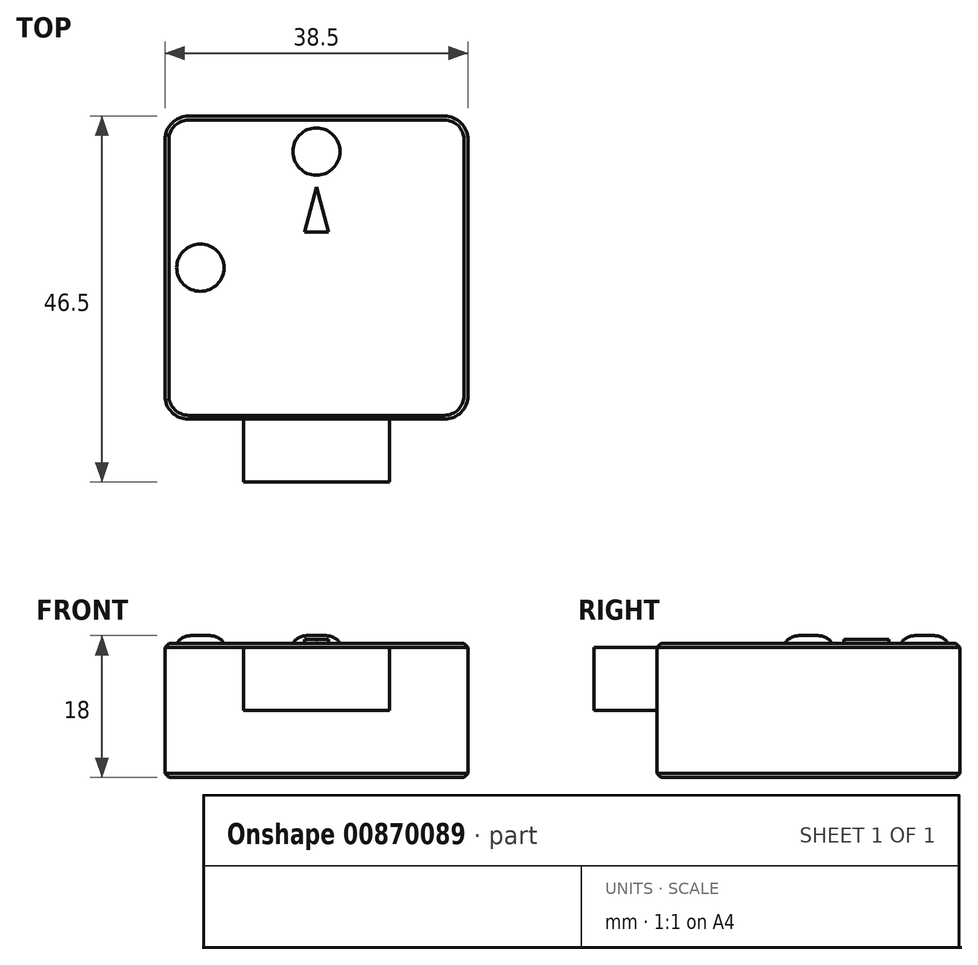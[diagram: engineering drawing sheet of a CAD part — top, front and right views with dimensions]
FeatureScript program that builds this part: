
annotation { "Feature Type Name" : "Feature", "Feature Type Description" : "" }
export const myFeature = defineFeature(function(context is Context, id is Id, definition is map)
    precondition{}
    {
        {
            var Q0;
            Q0=qCreatedBy(makeId("Top.planeOp"),FACE);
            var sketch = newSketch(context, id + "F0", { "sketchPlane" : qUnion([Q0])});
            skLineSegment(sketch, "E0.bottom", {"start": v(19.25, -19.25) * mm, "end": v(-19.25, -19.25) * mm});
            skLineSegment(sketch, "E0.top", {"start": v(19.25, 19.25) * mm, "end": v(-19.25, 19.25) * mm});
            skLineSegment(sketch, "E0.left", {"start": v(19.25, -19.25) * mm, "end": v(19.25, 19.25) * mm});
            skLineSegment(sketch, "E0.right", {"start": v(-19.25, -19.25) * mm, "end": v(-19.25, 19.25) * mm});
            skPoint(sketch, "E0.middle", {"position": v(0, 0) * mm});
            skCircle(sketch, "E1", {"center": v(0, 14.75) * mm, "radius": 3 * mm});
            skCircle(sketch, "E2", {"center": v(-14.75, 0) * mm, "radius": 3 * mm});
            skLineSegment(sketch, "E3", {"start": v(0, 19.25) * mm, "end": v(0, 17.75) * mm});
            skLineSegment(sketch, "E4", {"start": v(-19.25, 0) * mm, "end": v(-17.75, 0) * mm});
            skSolve(sketch);
        }
        {
            var Q0;
            {var subQ5=sQuery(id+"F0.wireOp",EDGE,"E0.bottom");Q0=makeQuery(id+"F0.imprint","IMPRINT",FACE,{"disambiguationData":[TD([[makeQuery(id+"F0.imprint","IMPRINT",EDGE,{"derivedFrom":subQ5}),-1.0]])]});}
            var Q1;
            Q1=makeQuery(id+"F0.imprint","IMPRINT",FACE,{"disambiguationData":[TD([[makeQuery(id+"F0.imprint","IMPRINT",EDGE,{"derivedFrom":sQuery(id+"F0.wireOp",EDGE,"E2")}),1.0]])]});
            var Q2;
            Q2=makeQuery(id+"F0.imprint","IMPRINT",FACE,{"disambiguationData":[TD([[makeQuery(id+"F0.imprint","IMPRINT",EDGE,{"derivedFrom":sQuery(id+"F0.wireOp",EDGE,"E1")}),1.0]])]});
            extrude(context, id + "F1", {"entities" : qUnion([Q0, Q1, Q2]), "depth" : 17 * mm, "offsetDistance" : 25 * mm});
        }
        {
            var Q0;
            Q0=makeQuery(id+"F1.opExtrude","CAP_FACE",FACE,{"disambiguationData":[OSD([sQuery(id+"F0.wireOp",EDGE,"E0.bottom"),sQuery(id+"F0.wireOp",EDGE,"E0.top"),sQuery(id+"F0.wireOp",EDGE,"E0.left"),sQuery(id+"F0.wireOp",EDGE,"E0.right"),sQuery(id+"F0.wireOp",EDGE,"9456177a-c9df-4c80-9ee9-95378c6d2fde.0"),sQuery(id+"F0.wireOp",EDGE,"9456177a-c9df-4c80-9ee9-95378c6d2fde.1"),sQuery(id+"F0.wireOp",EDGE,"9456177a-c9df-4c80-9ee9-95378c6d2fde.2")])],"isStart":false});
            var sketch = newSketch(context, id + "F2", { "sketchPlane" : qUnion([Q0])});
            skLineSegment(sketch, "E5.0", {"start": v(1.5, 4.5) * mm, "end": v(-1.5, 4.5) * mm});
            skLineSegment(sketch, "E5.1", {"start": v(-1.5, 4.5) * mm, "end": v(0, 10.23) * mm});
            skLineSegment(sketch, "E5.2", {"start": v(0, 10.23) * mm, "end": v(1.5, 4.5) * mm});
            skSolve(sketch);
        }
        {
            var Q0;
            Q0=makeQuery(id+"F2.imprint","IMPRINT",FACE,{"disambiguationData":[TD([[makeQuery(id+"F2.imprint","IMPRINT",EDGE,{"derivedFrom":sQuery(id+"F2.wireOp",EDGE,"E5.0")}),-1.0]])]});
            extrude(context, id + "F3", {"entities" : qUnion([Q0]), "operationType" : NewBodyOperationType.ADD, "depth" : .5 * mm, "offsetDistance" : 25 * mm});
        }
        {
            var Q0;
            Q0=makeQuery(id+"F0.imprint","IMPRINT",FACE,{"disambiguationData":[TD([[makeQuery(id+"F0.imprint","IMPRINT",EDGE,{"derivedFrom":sQuery(id+"F0.wireOp",EDGE,"E1")}),1.0]])]});
            var Q1;
            Q1=makeQuery(id+"F0.imprint","IMPRINT",FACE,{"disambiguationData":[TD([[makeQuery(id+"F0.imprint","IMPRINT",EDGE,{"derivedFrom":sQuery(id+"F0.wireOp",EDGE,"E2")}),1.0]])]});
            extrude(context, id + "F4", {"entities" : qUnion([Q0, Q1]), "operationType" : NewBodyOperationType.ADD, "depth" : 18 * mm, "offsetDistance" : 25 * mm});
        }
        {
            var Q0;
            Q0=makeQuery(id+"F4.opExtrude","CAP_FACE",FACE,{"disambiguationData":[OSD([sQuery(id+"F0.wireOp",EDGE,"E1")])],"isStart":false});
            var Q1;
            Q1=makeQuery(id+"F4.opExtrude","CAP_EDGE",EDGE,{"disambiguationData":[OSD([sQuery(id+"F0.wireOp",EDGE,"E2")])],"isStart":false});
            fillet(context, id + "F5", {"entities" : qUnion([Q0, Q1]), "radius" : 2 * mm, "tangentPropagation" : true, "allowEdgeOverflow" : false});
        }
        {
            var Q0;
            Q0=makeQuery(id+"F1.opExtrude","SWEPT_EDGE",EDGE,{"disambiguationData":[OSD([sQuery(id+"F0.wireOp",EDGE,"E0.bottom"),sQuery(id+"F0.wireOp",EDGE,"E0.left")])]});
            var Q1;
            Q1=makeQuery(id+"F1.opExtrude","SWEPT_EDGE",EDGE,{"disambiguationData":[OSD([sQuery(id+"F0.wireOp",EDGE,"E0.bottom"),sQuery(id+"F0.wireOp",EDGE,"E0.right")])]});
            var Q2;
            Q2=makeQuery(id+"F1.opExtrude","SWEPT_EDGE",EDGE,{"disambiguationData":[OSD([sQuery(id+"F0.wireOp",EDGE,"E0.top"),sQuery(id+"F0.wireOp",EDGE,"E0.right")])]});
            var Q3;
            Q3=makeQuery(id+"F1.opExtrude","SWEPT_EDGE",EDGE,{"disambiguationData":[OSD([sQuery(id+"F0.wireOp",EDGE,"E0.top"),sQuery(id+"F0.wireOp",EDGE,"E0.left")])]});
            fillet(context, id + "F6", {"entities" : qUnion([Q0, Q1, Q2, Q3]), "radius" : 3 * mm, "tangentPropagation" : true, "allowEdgeOverflow" : false});
        }
        {
            var Q0;
            Q0=makeQuery(id+"F1.opExtrude","CAP_EDGE",EDGE,{"disambiguationData":[OSD([sQuery(id+"F0.wireOp",EDGE,"E0.top")])],"isStart":false});
            var Q1;
            {var subQ0=sQuery(id+"F0.wireOp",EDGE,"E0.left");var subQ1=sQuery(id+"F0.wireOp",EDGE,"E0.top");Q1=makeQuery(id+"F6.opFillet","BLEND_EDGE",EDGE,{"blendedFrom":[makeQuery(id+"F1.opExtrude","SWEPT_EDGE",EDGE,{"disambiguationData":[OSD([subQ1,subQ0])]}),makeQuery(id+"F1.opExtrude","CAP_FACE",FACE,{"disambiguationData":[OSD([sQuery(id+"F0.wireOp",EDGE,"E0.bottom"),subQ1,subQ0,sQuery(id+"F0.wireOp",EDGE,"E0.right")])],"isStart":false})],"blendedInto":[makeQuery(id+"F1.opExtrude","CAP_FACE",FACE,{"disambiguationData":[OSD([sQuery(id+"F0.wireOp",EDGE,"E0.bottom"),subQ1,subQ0,sQuery(id+"F0.wireOp",EDGE,"E0.right")])],"isStart":false})]});}
            var Q2;
            Q2=makeQuery(id+"F1.opExtrude","CAP_EDGE",EDGE,{"disambiguationData":[OSD([sQuery(id+"F0.wireOp",EDGE,"E0.left")])],"isStart":false});
            var Q3;
            {var subQ0=sQuery(id+"F0.wireOp",EDGE,"E0.left");var subQ1=sQuery(id+"F0.wireOp",EDGE,"E0.bottom");Q3=makeQuery(id+"F6.opFillet","BLEND_EDGE",EDGE,{"blendedFrom":[makeQuery(id+"F1.opExtrude","SWEPT_EDGE",EDGE,{"disambiguationData":[OSD([subQ1,subQ0])]}),makeQuery(id+"F1.opExtrude","CAP_FACE",FACE,{"disambiguationData":[OSD([subQ1,sQuery(id+"F0.wireOp",EDGE,"E0.top"),subQ0,sQuery(id+"F0.wireOp",EDGE,"E0.right")])],"isStart":false})],"blendedInto":[makeQuery(id+"F1.opExtrude","CAP_FACE",FACE,{"disambiguationData":[OSD([subQ1,sQuery(id+"F0.wireOp",EDGE,"E0.top"),subQ0,sQuery(id+"F0.wireOp",EDGE,"E0.right")])],"isStart":false})]});}
            var Q4;
            Q4=makeQuery(id+"F1.opExtrude","CAP_EDGE",EDGE,{"disambiguationData":[OSD([sQuery(id+"F0.wireOp",EDGE,"E0.bottom")])],"isStart":false});
            var Q5;
            {var subQ0=sQuery(id+"F0.wireOp",EDGE,"E0.right");var subQ1=sQuery(id+"F0.wireOp",EDGE,"E0.bottom");Q5=makeQuery(id+"F6.opFillet","BLEND_EDGE",EDGE,{"blendedFrom":[makeQuery(id+"F1.opExtrude","SWEPT_EDGE",EDGE,{"disambiguationData":[OSD([subQ1,subQ0])]}),makeQuery(id+"F1.opExtrude","CAP_FACE",FACE,{"disambiguationData":[OSD([subQ1,sQuery(id+"F0.wireOp",EDGE,"E0.top"),sQuery(id+"F0.wireOp",EDGE,"E0.left"),subQ0])],"isStart":false})],"blendedInto":[makeQuery(id+"F1.opExtrude","CAP_FACE",FACE,{"disambiguationData":[OSD([subQ1,sQuery(id+"F0.wireOp",EDGE,"E0.top"),sQuery(id+"F0.wireOp",EDGE,"E0.left"),subQ0])],"isStart":false})]});}
            var Q6;
            Q6=makeQuery(id+"F1.opExtrude","CAP_EDGE",EDGE,{"disambiguationData":[OSD([sQuery(id+"F0.wireOp",EDGE,"E0.right")])],"isStart":false});
            var Q7;
            {var subQ0=sQuery(id+"F0.wireOp",EDGE,"E0.right");var subQ1=sQuery(id+"F0.wireOp",EDGE,"E0.top");Q7=makeQuery(id+"F6.opFillet","BLEND_EDGE",EDGE,{"blendedFrom":[makeQuery(id+"F1.opExtrude","SWEPT_EDGE",EDGE,{"disambiguationData":[OSD([subQ1,subQ0])]}),makeQuery(id+"F1.opExtrude","CAP_FACE",FACE,{"disambiguationData":[OSD([sQuery(id+"F0.wireOp",EDGE,"E0.bottom"),subQ1,sQuery(id+"F0.wireOp",EDGE,"E0.left"),subQ0])],"isStart":false})],"blendedInto":[makeQuery(id+"F1.opExtrude","CAP_FACE",FACE,{"disambiguationData":[OSD([sQuery(id+"F0.wireOp",EDGE,"E0.bottom"),subQ1,sQuery(id+"F0.wireOp",EDGE,"E0.left"),subQ0])],"isStart":false})]});}
            var Q8;
            Q8=makeQuery(id+"F1.opExtrude","CAP_EDGE",EDGE,{"disambiguationData":[OSD([sQuery(id+"F0.wireOp",EDGE,"E0.bottom")])],"isStart":true});
            chamfer(context, id + "F7", {"entities" : qUnion([Q0, Q1, Q2, Q3, Q4, Q5, Q6, Q7, Q8]), "width" : .5 * mm, "tangentPropagation" : true});
        }
        {
            var Q0;
            Q0=makeQuery(id+"F1.opExtrude","SWEPT_FACE",FACE,{"disambiguationData":[OSD([sQuery(id+"F0.wireOp",EDGE,"E0.bottom")])]});
            var sketch = newSketch(context, id + "F8", { "sketchPlane" : qUnion([Q0])});
            skLineSegment(sketch, "E6", {"start": v(-16.25, 16.5) * mm, "end": v(-16.25, 0.5) * mm, "construction": true});
            skLineSegment(sketch, "E7", {"start": v(-16.25, 0.5) * mm, "end": v(-16.25, 8.5) * mm, "construction": true});
            skLineSegment(sketch, "E8", {"start": v(-16.25, 8.5) * mm, "end": v(16.25, 8.5) * mm, "construction": true});
            skLineSegment(sketch, "E9", {"start": v(16.25, 16.5) * mm, "end": v(9.25, 16.5) * mm, "construction": true});
            skLineSegment(sketch, "E10", {"start": v(9.25, 16.5) * mm, "end": v(9.25, 8.5) * mm});
            skLineSegment(sketch, "E11", {"start": v(-16.25, 16.5) * mm, "end": v(-9.25, 16.5) * mm, "construction": true});
            skLineSegment(sketch, "E12", {"start": v(-9.25, 16.5) * mm, "end": v(-9.25, 8.5) * mm});
            skLineSegment(sketch, "E13", {"start": v(-9.25, 8.5) * mm, "end": v(9.25, 8.5) * mm});
            skLineSegment(sketch, "E14", {"start": v(-9.25, 16.5) * mm, "end": v(9.25, 16.5) * mm});
            skSolve(sketch);
        }
        {
            var Q0;
            Q0=makeQuery(id+"F8.imprint","IMPRINT",FACE,{"disambiguationData":[TD([[makeQuery(id+"F8.imprint","IMPRINT",EDGE,{"derivedFrom":sQuery(id+"F8.wireOp",EDGE,"E10")}),-1.0]])]});
            extrude(context, id + "F9", {"entities" : qUnion([Q0]), "operationType" : NewBodyOperationType.ADD, "depth" : 8 * mm, "offsetDistance" : 25 * mm});
        }
    });
